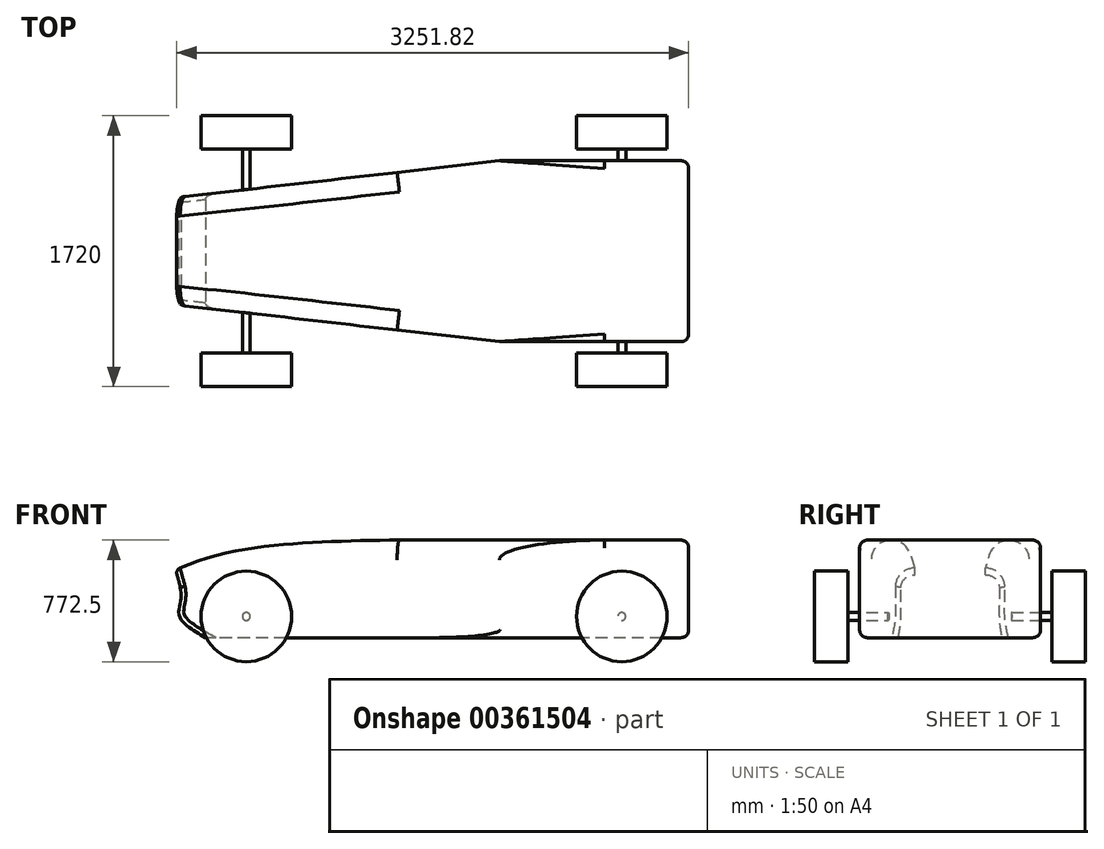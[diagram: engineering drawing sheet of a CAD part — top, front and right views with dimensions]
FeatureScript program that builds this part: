
annotation { "Feature Type Name" : "Feature", "Feature Type Description" : "" }
export const myFeature = defineFeature(function(context is Context, id is Id, definition is map)
    precondition{}
    {
        {
            var Q0;
            Q0=qCreatedBy(makeId("Front.planeOp"),FACE);
            cPlane(context, id + "F0", {"entities" : qUnion([Q0]), "cplaneType" : CPlaneType.OFFSET, "offset" : 860 * mm, "width" : 150 * mm, "height" : 150 * mm});
        }
        {
            var Q0;
            Q0=qCreatedBy(id+"F0.planeOp",FACE);
            var sketch = newSketch(context, id + "F1", { "sketchPlane" : qUnion([Q0])});
            skCircle(sketch, "E0", {"center": v(-1192.5, 0) * mm, "radius": 287.5 * mm});
            skSolve(sketch);
        }
        {
            var Q0;
            Q0 = qSketchRegion(id + "F1", true);
            extrude(context, id + "F2", {"entities" : qUnion([Q0]), "oppositeDirection" : true, "depth" : 212.5 * mm});
        }
        {
            var Q0;
            Q0=makeQuery(id+"F2.opExtrude","SWEPT_BODY",BODY,{"disambiguationData":[OSD([sQuery(id+"F1.wireOp",EDGE,"E0")])]});
            var Q1;
            Q1=qCreatedBy(makeId("Right.planeOp"),FACE);
            mirror(context, id + "F3", {"entities" : qUnion([Q0]), "mirrorPlane" : qUnion([Q1])});
        }
        {
            var Q0;
            Q0=makeQuery(id+"F2.opExtrude","SWEPT_BODY",BODY,{"disambiguationData":[OSD([sQuery(id+"F1.wireOp",EDGE,"E0")])]});
            var Q1;
            Q1=makeQuery(id+"F3.opPattern","COPY",BODY,{"derivedFrom":makeQuery(id+"F2.opExtrude","SWEPT_BODY",BODY,{"disambiguationData":[OSD([sQuery(id+"F1.wireOp",EDGE,"E0")])]}),"instanceName":"1"});
            var Q2;
            Q2=qCreatedBy(makeId("Front.planeOp"),FACE);
            mirror(context, id + "F4", {"entities" : qUnion([Q0, Q1]), "mirrorPlane" : qUnion([Q2])});
        }
        {
            var Q0;
            Q0=qCreatedBy(makeId("Top.planeOp"),FACE);
            var sketch = newSketch(context, id + "F5", { "sketchPlane" : qUnion([Q0])});
            skLineSegment(sketch, "E1", {"start": v(1617.5, 0) * mm, "end": v(1617.5, 575) * mm});
            skLineSegment(sketch, "E2", {"start": v(1617.5, 575) * mm, "end": v(417.5, 575) * mm});
            skLineSegment(sketch, "E3", {"start": v(417.5, 575) * mm, "end": v(-1642.5, 340.3) * mm});
            skLineSegment(sketch, "E4", {"start": v(-1642.5, 340.3) * mm, "end": v(-1642.5, 0) * mm});
            skLineSegment(sketch, "E5", {"start": v(-1642.5, 0) * mm, "end": v(1617.5, 0) * mm, "construction": true});
            skLineSegment(sketch, "E6", {"start": v(1192.5, 860) * mm, "end": v(1192.5, 647.5) * mm, "construction": true});
            skLineSegment(sketch, "E7", {"start": v(-1192.5, 860) * mm, "end": v(-1192.5, 647.5) * mm, "construction": true});
            skLineSegment(sketch, "E8.MirrorCS", {"start": v(-1642.5, -340.3) * mm, "end": v(-1642.5, 0) * mm});
            skLineSegment(sketch, "E9.MirrorCS", {"start": v(417.5, -575) * mm, "end": v(-1642.5, -340.3) * mm});
            skLineSegment(sketch, "E10.MirrorCS", {"start": v(1617.5, -575) * mm, "end": v(417.5, -575) * mm});
            skLineSegment(sketch, "E11.MirrorCS", {"start": v(1617.5, 0) * mm, "end": v(1617.5, -575) * mm});
            skSolve(sketch);
        }
        {
            var Q0;
            Q0=makeQuery(id+"F5.imprint","IMPRINT",FACE,{"disambiguationData":[TD([[makeQuery(id+"F5.imprint","IMPRINT",EDGE,{"derivedFrom":sQuery(id+"F5.wireOp",EDGE,"E1")}),1.0]])]});
            extrude(context, id + "F6", {"entities" : qUnion([Q0]), "depth" : 485 * mm, "hasSecondDirection" : true, "secondDirectionOppositeDirection" : true, "secondDirectionDepth" : 135 * mm});
        }
        {
            var Q0;
            Q0=qCreatedBy(makeId("Front.planeOp"),FACE);
            var sketch = newSketch(context, id + "F7", { "sketchPlane" : qUnion([Q0])});
            skFitSpline(sketch, "E12", {"points": [v(-1642.5, 295.65) * mm, v(-1257.97, 416.82) * mm, v(-113.86, 485) * mm], "startDerivative": vector(1006.8, 410) * mm, "endDerivative": vector(2138.2, -8.23) * mm});
            skFitSpline(sketch, "E13", {"points": [v(-1642.5, 295.65) * mm, v(-1607.5, 120.89) * mm, v(-1616.81, 0) * mm, v(-1451.37, -135) * mm], "startDerivative": vector(170.43, -528.88) * mm, "endDerivative": vector(593.36, -339.69) * mm});
            skLineSegment(sketch, "E14", {"start": v(-1451.37, -135) * mm, "end": v(-1451.37, -228.64) * mm});
            skLineSegment(sketch, "E15", {"start": v(-1451.37, -228.64) * mm, "end": v(-1682.06, -228.64) * mm});
            skLineSegment(sketch, "E16", {"start": v(-1682.06, -228.64) * mm, "end": v(-1682.06, 561.29) * mm});
            skLineSegment(sketch, "E17", {"start": v(-1682.06, 561.29) * mm, "end": v(-113.86, 561.29) * mm});
            skLineSegment(sketch, "E18", {"start": v(-113.86, 561.29) * mm, "end": v(-113.86, 485) * mm});
            skSolve(sketch);
        }
        {
            var Q0;
            Q0 = qSketchRegion(id + "F7", true);
            extrude(context, id + "F8", {"entities" : qUnion([Q0]), "operationType" : NewBodyOperationType.REMOVE, "endBound" : BoundingType.THROUGH_ALL, "oppositeDirection" : true, "depth" : 25 * mm, "hasSecondDirection" : true, "secondDirectionBound" : SecondDirectionBoundingType.THROUGH_ALL, "secondDirectionOppositeDirection" : false, "secondDirectionDepth" : 25 * mm});
        }
        {
            var Q0;
            Q0=makeQuery(id+"F8.boolean.opBoolean","INTERSECT",EDGE,{"derivedFrom":[makeQuery(id+"F6.opExtrude","SWEPT_FACE",FACE,{"disambiguationData":[OSD([sQuery(id+"F5.wireOp",EDGE,"E3")])]}),makeQuery(id+"F8.opExtrude","SWEPT_FACE",FACE,{"disambiguationData":[OSD([sQuery(id+"F7.wireOp",EDGE,"E12")])]})]});
            var Q1;
            Q1=makeQuery(id+"F8.boolean.opBoolean","INTERSECT",EDGE,{"derivedFrom":[makeQuery(id+"F6.opExtrude","SWEPT_FACE",FACE,{"disambiguationData":[OSD([sQuery(id+"F5.wireOp",EDGE,"E9.MirrorCS")])]}),makeQuery(id+"F8.opExtrude","SWEPT_FACE",FACE,{"disambiguationData":[OSD([sQuery(id+"F7.wireOp",EDGE,"E12")])]})]});
            var Q2;
            Q2=makeQuery(id+"F6.opExtrude","CAP_EDGE",EDGE,{"disambiguationData":[OSD([sQuery(id+"F5.wireOp",EDGE,"E3")])],"isStart":false});
            var Q3;
            Q3=makeQuery(id+"F6.opExtrude","CAP_EDGE",EDGE,{"disambiguationData":[OSD([sQuery(id+"F5.wireOp",EDGE,"E9.MirrorCS")])],"isStart":false});
            fillet(context, id + "F9", {"entities" : qUnion([Q0, Q1, Q2, Q3]), "radius" : 125 * mm, "tangentPropagation" : true, "allowEdgeOverflow" : false});
        }
        {
            var Q0;
            Q0=makeQuery(id+"F8.boolean.opBoolean","COPY",EDGE,{"derivedFrom":makeQuery(id+"F8.opExtrude","SWEPT_EDGE",EDGE,{"disambiguationData":[OSD([sQuery(id+"F7.wireOp",EDGE,"E12"),sQuery(id+"F7.wireOp",EDGE,"E13")])]})});
            var Q1;
            Q1=makeQuery(id+"F9.opFillet","BLEND_EDGE",EDGE,{"blendedFrom":[makeQuery(id+"F8.boolean.opBoolean","INTERSECT",EDGE,{"derivedFrom":[makeQuery(id+"F6.opExtrude","SWEPT_FACE",FACE,{"disambiguationData":[OSD([sQuery(id+"F5.wireOp",EDGE,"E3")])]}),makeQuery(id+"F8.opExtrude","SWEPT_FACE",FACE,{"disambiguationData":[OSD([sQuery(id+"F7.wireOp",EDGE,"E12")])]})]}),makeQuery(id+"F8.boolean.opBoolean","COPY",FACE,{"derivedFrom":makeQuery(id+"F8.opExtrude","SWEPT_FACE",FACE,{"disambiguationData":[OSD([sQuery(id+"F7.wireOp",EDGE,"E13")])]})})],"blendedInto":[makeQuery(id+"F8.boolean.opBoolean","COPY",FACE,{"derivedFrom":makeQuery(id+"F8.opExtrude","SWEPT_FACE",FACE,{"disambiguationData":[OSD([sQuery(id+"F7.wireOp",EDGE,"E13")])]})})]});
            fillet(context, id + "F10", {"entities" : qUnion([Q0, Q1]), "radius" : 35 * mm, "tangentPropagation" : true, "allowEdgeOverflow" : false});
        }
        {
            var Q0;
            Q0=makeQuery(id+"F6.opExtrude","SWEPT_EDGE",EDGE,{"disambiguationData":[OSD([sQuery(id+"F5.wireOp",EDGE,"E1"),sQuery(id+"F5.wireOp",EDGE,"E2")])]});
            var Q1;
            Q1=makeQuery(id+"F6.opExtrude","SWEPT_EDGE",EDGE,{"disambiguationData":[OSD([sQuery(id+"F5.wireOp",EDGE,"E10.MirrorCS"),sQuery(id+"F5.wireOp",EDGE,"E11.MirrorCS")])]});
            var Q2;
            Q2=makeQuery(id+"F6.opExtrude","CAP_EDGE",EDGE,{"disambiguationData":[OSD([sQuery(id+"F5.wireOp",EDGE,"E1"),sQuery(id+"F5.wireOp",EDGE,"E11.MirrorCS")])],"isStart":false});
            var Q3;
            Q3=makeQuery(id+"F6.opExtrude","CAP_EDGE",EDGE,{"disambiguationData":[OSD([sQuery(id+"F5.wireOp",EDGE,"E1"),sQuery(id+"F5.wireOp",EDGE,"E11.MirrorCS")])],"isStart":true});
            var Q4;
            Q4=makeQuery(id+"F6.opExtrude","CAP_EDGE",EDGE,{"disambiguationData":[OSD([sQuery(id+"F5.wireOp",EDGE,"E2")])],"isStart":false});
            var Q5;
            Q5=makeQuery(id+"F6.opExtrude","CAP_EDGE",EDGE,{"disambiguationData":[OSD([sQuery(id+"F5.wireOp",EDGE,"E10.MirrorCS")])],"isStart":false});
            var Q6;
            Q6=makeQuery(id+"F6.opExtrude","CAP_EDGE",EDGE,{"disambiguationData":[OSD([sQuery(id+"F5.wireOp",EDGE,"E10.MirrorCS")])],"isStart":true});
            var Q7;
            Q7=makeQuery(id+"F6.opExtrude","CAP_EDGE",EDGE,{"disambiguationData":[OSD([sQuery(id+"F5.wireOp",EDGE,"E2")])],"isStart":true});
            fillet(context, id + "F11", {"entities" : qUnion([Q0, Q1, Q2, Q3, Q4, Q5, Q6, Q7]), "radius" : 50 * mm, "tangentPropagation" : true, "allowEdgeOverflow" : false});
        }
        {
            var Q0;
            Q0=makeQuery(id+"F4.opPattern","COPY",FACE,{"derivedFrom":makeQuery(id+"F2.opExtrude","CAP_FACE",FACE,{"disambiguationData":[OSD([sQuery(id+"F1.wireOp",EDGE,"E0")])],"isStart":false}),"instanceName":"1"});
            var sketch = newSketch(context, id + "F12", { "sketchPlane" : qUnion([Q0])});
            skCircle(sketch, "E19", {"center": v(-1192.5, 0) * mm, "radius": 25 * mm});
            skCircle(sketch, "E20", {"center": v(1192.5, 0) * mm, "radius": 25 * mm});
            skSolve(sketch);
        }
        {
            var Q0;
            Q0 = qSketchRegion(id + "F12", true);
            var Q1;
            Q1=makeQuery(id+"F2.opExtrude","CAP_FACE",FACE,{"disambiguationData":[OSD([sQuery(id+"F1.wireOp",EDGE,"E0")])],"isStart":false});
            var Q2;
            Q2=makeQuery(id+"F3.opPattern","COPY",BODY,{"derivedFrom":makeQuery(id+"F2.opExtrude","SWEPT_BODY",BODY,{"disambiguationData":[OSD([sQuery(id+"F1.wireOp",EDGE,"E0")])]}),"instanceName":"1"});
            extrude(context, id + "F13", {"entities" : qUnion([Q0]), "operationType" : NewBodyOperationType.ADD, "endBound" : BoundingType.UP_TO_SURFACE, "endBoundEntityFace" : qUnion([Q1]), "endBoundEntityBody" : qUnion([Q2]), "depth" : 25 * mm});
        }
    });
